# Revit family: LSQ
name_source: partatom
category: Lighting Fixtures
revit_build: Autodesk Revit 2013 (Build: 20130531_2115(x64)
units: mm (PartAtom-declared; Revit-internal decimal feet)

## types (4) — shared parameters
Assembly Code = D5020200
Color Filter = 16777215
Default Elevation = 48 "
Description = Lumasquare luminaires provide a seamless blend of performance, visual comfort, controls and accessory options in an elegant/low profile form factor to enhance the environment in which they occupy.
Dimming Lamp Color Temperature Shift = <None>
Emit Shape Visible in Rendering = No
Fixture Glass = Hubbell - White Glass
Hardware Finish = Powdercoat - Hubbell - Gray
Lamp = LED Lamp
Load Classification = Lighting
Manufacturer = Hubbell Outdoor Lighting
Model = LSQ
Photometric Notes = More IES files download on Photometric Web Link
Photometric Web Link = https://www.hubbell.com
Power factor = 1
Product Documentation Link = https://hubbellcdn.com
Product Page URL = https://www.hubbell.com
Tilt Angle = -90.00°
URL = https://www.hubbell.com
Voltage = 120 V
Warranty = Five year warranty
Wattage Comments = 25,40,55&70

## per-type parameters (varying)
| type | Apparent Load | Emit from Rectangle Length | Emit from Rectangle Width | LSQ1 | LSQ2 | Photometric Web File | Watts | zz Length 1 | zz Length 2 | zz Length 3 |
| LSQ2-70-3K8-UNV-X | 70 VA | 13.8 " | 13.8 " | No | Yes | LSQ2-70-3K8-UNV-X.IES | 70 W | 14.8 " | 6 " | 4 " |
| LSQ2-55-5K7-UNV-X | 55 VA | 13.8 " | 13.8 " | No | Yes | LSQ2-55-5K7-UNV-X.IES | 55 W | 14.8 " | 6 " | 4 " |
| LSQ1-40-4K7-UNV-X | 40 VA | 9 " | 9 " | Yes | No | LSQ1-40-4K7-UNV-X.IES | 40 W | 10 " | 4 " | 3 " |
| LSQ1-25-3K8-UNV-X | 25 VA | 9 " | 9 " | Yes | No | LSQ1-25-3K8-UNV-X.IES | 25 W | 10 " | 4 " | 3 " |

## geometry (parser evidence)
native form markers: Blend x1, Sweep x1
no freeform markers — native parametric forms only
